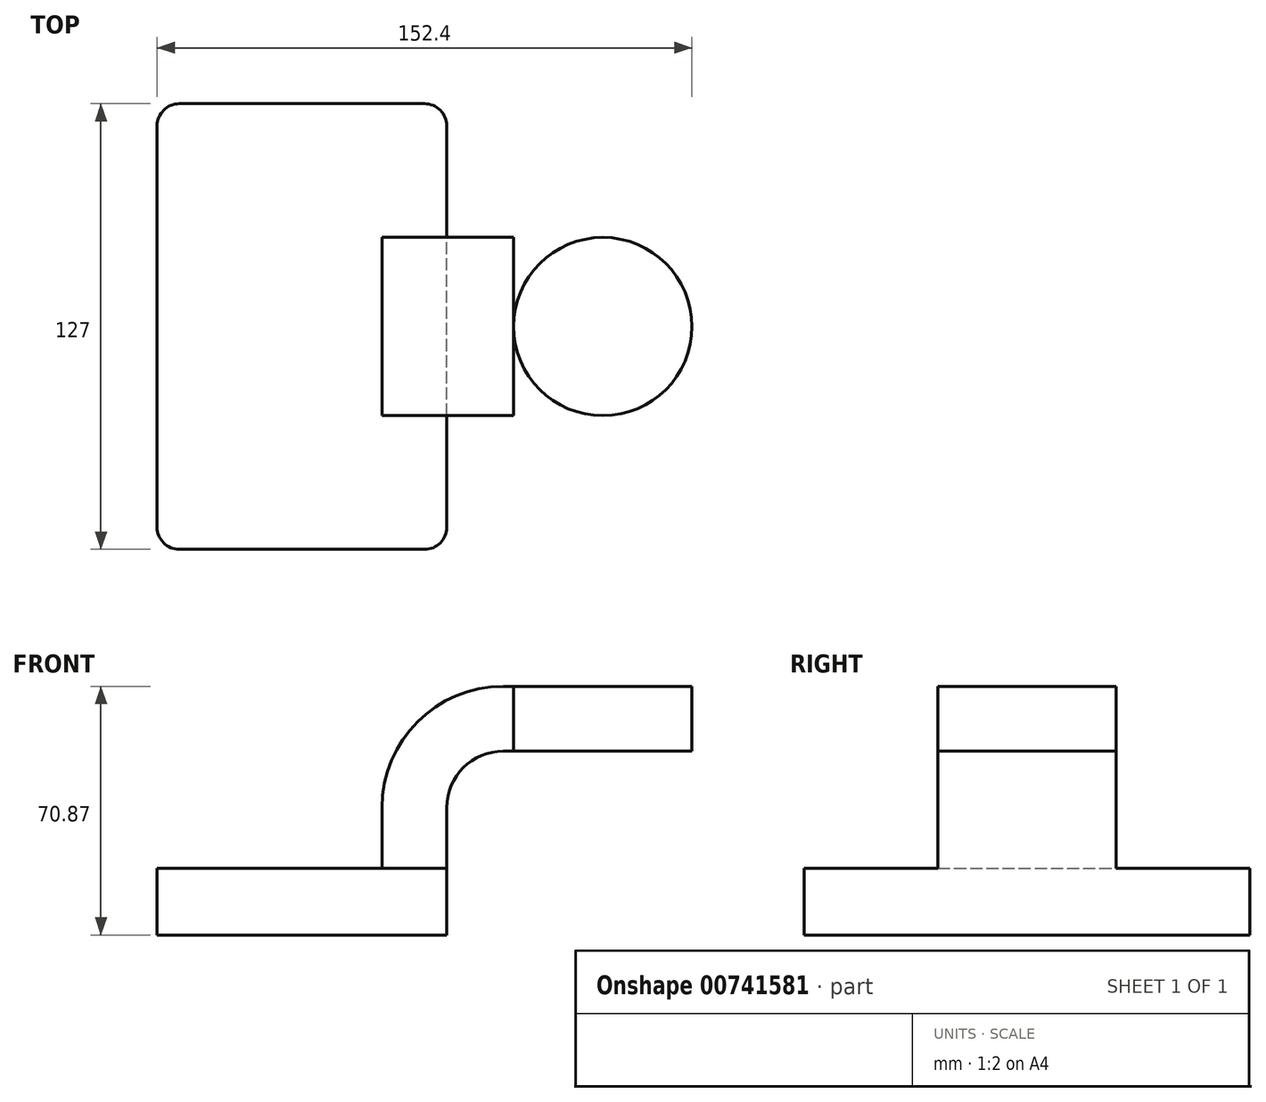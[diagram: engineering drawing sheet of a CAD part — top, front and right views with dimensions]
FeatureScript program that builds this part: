
annotation { "Feature Type Name" : "Feature", "Feature Type Description" : "" }
export const myFeature = defineFeature(function(context is Context, id is Id, definition is map)
    precondition{}
    {
        {
            var Q0;
            Q0=qCreatedBy(makeId("Front.planeOp"),FACE);
            var sketch = newSketch(context, id + "F0", { "sketchPlane" : qUnion([Q0])});
            skLineSegment(sketch, "E0.bottom", {"start": v(-41.28, 9.52) * mm, "end": v(41.27, 9.53) * mm});
            skLineSegment(sketch, "E0.top", {"start": v(-41.28, -9.53) * mm, "end": v(41.28, -9.53) * mm});
            skLineSegment(sketch, "E0.left", {"start": v(-41.28, 9.52) * mm, "end": v(-41.27, -9.53) * mm});
            skLineSegment(sketch, "E0.right", {"start": v(41.28, 9.53) * mm, "end": v(41.28, -9.52) * mm});
            skPoint(sketch, "E0.middle", {"position": v(0, 0) * mm});
            skLineSegment(sketch, "E1.bottom", {"start": v(60.32, 61.34) * mm, "end": v(111.12, 61.34) * mm});
            skLineSegment(sketch, "E1.top", {"start": v(60.32, 32.98) * mm, "end": v(111.12, 32.98) * mm});
            skLineSegment(sketch, "E1.left", {"start": v(60.33, 61.34) * mm, "end": v(60.33, 32.98) * mm});
            skLineSegment(sketch, "E1.right", {"start": v(111.12, 61.34) * mm, "end": v(111.12, 32.98) * mm});
            skPoint(sketch, "E1.middle", {"position": v(85.72, 47.16) * mm});
            skLineSegment(sketch, "E2", {"start": v(41.27, 9.53) * mm, "end": v(41.27, 26.76) * mm});
            skArc(sketch, "E3", {"start": v(41.28, 26.76) * mm, "mid": v(46, 38.15) * mm, "end": v(57.4, 42.88) * mm});
            skLineSegment(sketch, "E4", {"start": v(57.4, 42.88) * mm, "end": v(85.73, 42.88) * mm});
            skLineSegment(sketch, "E5.0", {"start": v(57.4, 61.34) * mm, "end": v(85.73, 61.34) * mm});
            skArc(sketch, "E5.1", {"start": v(22.81, 26.76) * mm, "mid": v(32.94, 51.21) * mm, "end": v(57.4, 61.34) * mm});
            skLineSegment(sketch, "E5.2", {"start": v(22.81, 9.53) * mm, "end": v(22.81, 26.76) * mm});
            skLineSegment(sketch, "E6", {"start": v(85.73, 42.88) * mm, "end": v(85.73, 61.34) * mm});
            skLineSegment(sketch, "E7", {"start": v(85.73, 42.88) * mm, "end": v(85.73, 32.98) * mm});
            skFitSpline(sketch, "E8", {"points": [v(-41.28, 9.53) * mm, v(60.32, 61.34) * mm], "startDerivative": vector(91.52, 92.82) * mm, "endDerivative": vector(106.56, -5.9) * mm});
            skSolve(sketch);
        }
        {
            var Q0;
            Q0=makeQuery(id+"F0.imprint","IMPRINT",FACE,{"disambiguationData":[TD([[makeQuery(id+"F0.imprint","IMPRINT",EDGE,{"derivedFrom":sQuery(id+"F0.wireOp",EDGE,"E0.top")}),1.0]])]});
            extrude(context, id + "F1", {"entities" : qUnion([Q0]), "endBound" : BoundingType.SYMMETRIC, "depth" : 127 * mm, "offsetDistance" : 25.4 * mm});
        }
        {
            var Q0;
            {var subQ1=sQuery(id+"F0.wireOp",EDGE,"E2");Q0=makeQuery(id+"F0.imprint","IMPRINT",FACE,{"disambiguationData":[TD([[makeQuery(id+"F0.imprint","IMPRINT",EDGE,{"derivedFrom":subQ1}),1.0]])]});}
            extrude(context, id + "F2", {"entities" : qUnion([Q0]), "operationType" : NewBodyOperationType.ADD, "endBound" : BoundingType.SYMMETRIC, "depth" : 50.8 * mm, "offsetDistance" : 25.4 * mm});
        }
        {
            var Q0;
            {var subQ0=sQuery(id+"F0.wireOp",EDGE,"E5.1");Q0=makeQuery(id+"F0.imprint","IMPRINT",FACE,{"disambiguationData":[TD([[makeQuery(id+"F0.imprint","IMPRINT",EDGE,{"derivedFrom":subQ0}),1.0]])]});}
            extrude(context, id + "F3", {"entities" : qUnion([Q0]), "operationType" : NewBodyOperationType.ADD, "endBound" : BoundingType.SYMMETRIC, "depth" : 15.88 * mm, "offsetDistance" : 25.4 * mm});
        }
        {
            var Q0;
            {var subQ5=sQuery(id+"F0.wireOp",EDGE,"E6");Q0=makeQuery(id+"F0.imprint","IMPRINT",FACE,{"disambiguationData":[TD([[makeQuery(id+"F0.imprint","IMPRINT",EDGE,{"derivedFrom":subQ5}),1.0]])]});}
            var Q1;
            Q1=sQuery(id+"F0.wireOp",EDGE,"E6");
            revolve(context, id + "F4", {"operationType" : NewBodyOperationType.ADD, "surfaceOperationType" : NewSurfaceOperationType.NEW, "entities" : qUnion([Q0]), "axis" : qUnion([Q1]), "revolveType" : RevolveType.FULL});
        }
        {
            var Q0;
            Q0=makeQuery(id+"F1.opExtrude","CAP_EDGE",EDGE,{"disambiguationData":[OSD([sQuery(id+"F0.wireOp",EDGE,"E0.right")])],"isStart":false});
            var Q1;
            Q1=makeQuery(id+"F1.opExtrude","CAP_EDGE",EDGE,{"disambiguationData":[OSD([sQuery(id+"F0.wireOp",EDGE,"E0.left")])],"isStart":false});
            var Q2;
            Q2=makeQuery(id+"F1.opExtrude","CAP_EDGE",EDGE,{"disambiguationData":[OSD([sQuery(id+"F0.wireOp",EDGE,"E0.left")])],"isStart":true});
            var Q3;
            Q3=makeQuery(id+"F1.opExtrude","CAP_EDGE",EDGE,{"disambiguationData":[OSD([sQuery(id+"F0.wireOp",EDGE,"E0.right")])],"isStart":true});
            fillet(context, id + "F5", {"entities" : qUnion([Q0, Q1, Q2, Q3]), "radius" : 6.35 * mm, "tangentPropagation" : true, "allowEdgeOverflow" : false});
        }
    });
